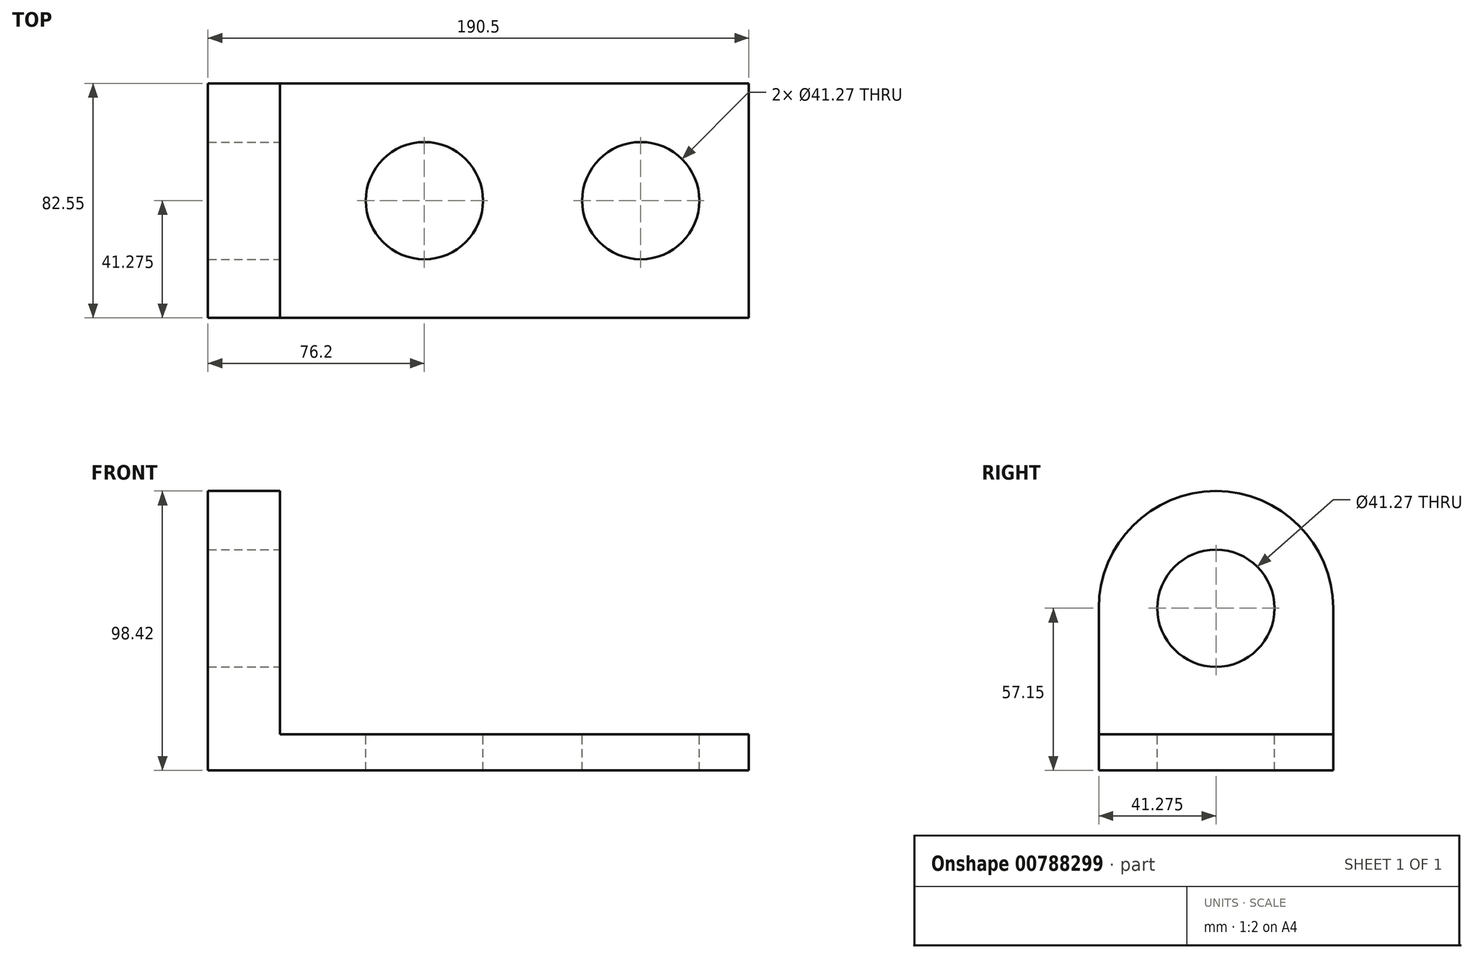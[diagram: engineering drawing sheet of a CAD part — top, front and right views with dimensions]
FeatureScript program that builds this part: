
annotation { "Feature Type Name" : "Feature", "Feature Type Description" : "" }
export const myFeature = defineFeature(function(context is Context, id is Id, definition is map)
    precondition{}
    {
        {
            var Q0;
            Q0=qCreatedBy(makeId("Front.planeOp"),FACE);
            var sketch = newSketch(context, id + "F0", { "sketchPlane" : qUnion([Q0])});
            skLineSegment(sketch, "E0", {"start": v(0, 0) * mm, "end": v(190.5, 0) * mm});
            skLineSegment(sketch, "E1", {"start": v(190.5, 0) * mm, "end": v(190.5, 12.7) * mm});
            skLineSegment(sketch, "E2", {"start": v(190.5, 12.7) * mm, "end": v(25.4, 12.7) * mm});
            skLineSegment(sketch, "E3", {"start": v(25.4, 12.7) * mm, "end": v(25.4, 114.3) * mm});
            skLineSegment(sketch, "E4", {"start": v(25.4, 114.3) * mm, "end": v(0, 114.3) * mm});
            skLineSegment(sketch, "E5", {"start": v(0, 114.3) * mm, "end": v(0, 0) * mm});
            skSolve(sketch);
        }
        {
            var Q0;
            Q0 = qSketchRegion(id + "F0", true);
            extrude(context, id + "F1", {"entities" : qUnion([Q0]), "depth" : 82.55 * mm, "offsetDistance" : 25.4 * mm});
        }
        {
            var Q0;
            Q0=makeQuery(id+"F1.opExtrude","SWEPT_FACE",FACE,{"disambiguationData":[OSD([sQuery(id+"F0.wireOp",EDGE,"E3")])]});
            var sketch = newSketch(context, id + "F2", { "sketchPlane" : qUnion([Q0])});
            skLineSegment(sketch, "E6", {"start": v(-82.55, 12.7) * mm, "end": v(-82.55, 57.15) * mm, "construction": true});
            skLineSegment(sketch, "E7", {"start": v(0, 12.7) * mm, "end": v(0, 57.15) * mm, "construction": true});
            skArc(sketch, "E8", {"start": v(0, 57.15) * mm, "mid": v(-41.28, 98.43) * mm, "end": v(-82.55, 57.15) * mm});
            skSolve(sketch);
        }
        {
            var Q0;
            {var subQ0=sQuery(id+"F2.wireOp",EDGE,"E8");Q0=makeQuery(id+"F2.imprint","IMPRINT",FACE,{"disambiguationData":[TD([[makeQuery(id+"F2.imprint","IMPRINT",EDGE,{"derivedFrom":subQ0}),-1.0]])]});}
            extrude(context, id + "F3", {"entities" : qUnion([Q0]), "operationType" : NewBodyOperationType.REMOVE, "oppositeDirection" : true, "depth" : 25.4 * mm, "offsetDistance" : 25.4 * mm});
        }
        {
            var Q0;
            Q0=makeQuery(id+"F1.opExtrude","SWEPT_FACE",FACE,{"disambiguationData":[OSD([sQuery(id+"F0.wireOp",EDGE,"E3")])]});
            var sketch = newSketch(context, id + "F4", { "sketchPlane" : qUnion([Q0])});
            skLineSegment(sketch, "E9", {"start": v(-82.55, 12.7) * mm, "end": v(-82.55, 57.15) * mm, "construction": true});
            skLineSegment(sketch, "E10", {"start": v(-82.55, 57.15) * mm, "end": v(-41.28, 57.15) * mm, "construction": true});
            skLineSegment(sketch, "E11", {"start": v(-41.28, 57.15) * mm, "end": v(0, 57.15) * mm, "construction": true});
            skLineSegment(sketch, "E12", {"start": v(0, 57.15) * mm, "end": v(0, 12.7) * mm, "construction": true});
            skCircle(sketch, "E13", {"center": v(-41.28, 57.15) * mm, "radius": 20.64 * mm});
            skSolve(sketch);
        }
        {
            var Q0;
            Q0=makeQuery(id+"F4.imprint","IMPRINT",FACE,{"disambiguationData":[TD([[makeQuery(id+"F4.imprint","IMPRINT",EDGE,{"derivedFrom":sQuery(id+"F4.wireOp",EDGE,"E13")}),1.0]])]});
            extrude(context, id + "F5", {"entities" : qUnion([Q0]), "operationType" : NewBodyOperationType.REMOVE, "endBound" : BoundingType.UP_TO_NEXT, "oppositeDirection" : true, "depth" : 25.4 * mm, "offsetDistance" : 25.4 * mm});
        }
        {
            var Q0;
            Q0=makeQuery(id+"F1.opExtrude","SWEPT_FACE",FACE,{"disambiguationData":[OSD([sQuery(id+"F0.wireOp",EDGE,"E2")])]});
            var sketch = newSketch(context, id + "F6", { "sketchPlane" : qUnion([Q0])});
            skLineSegment(sketch, "E14", {"start": v(190.5, -41.28) * mm, "end": v(152.4, -41.28) * mm, "construction": true});
            skLineSegment(sketch, "E15", {"start": v(152.4, -41.28) * mm, "end": v(76.2, -41.28) * mm, "construction": true});
            skCircle(sketch, "E16", {"center": v(76.2, -41.28) * mm, "radius": 20.64 * mm, "construction": true});
            skCircle(sketch, "E17", {"center": v(152.4, -41.28) * mm, "radius": 20.64 * mm, "construction": true});
            skCircle(sketch, "E18", {"center": v(76.2, -41.28) * mm, "radius": 20.64 * mm});
            skCircle(sketch, "E19", {"center": v(152.4, -41.28) * mm, "radius": 20.64 * mm});
            skSolve(sketch);
        }
        {
            var Q0;
            Q0 = qSketchRegion(id + "F6", true);
            extrude(context, id + "F7", {"entities" : qUnion([Q0]), "operationType" : NewBodyOperationType.REMOVE, "oppositeDirection" : true, "depth" : 25.4 * mm, "offsetDistance" : 25.4 * mm});
        }
    });
